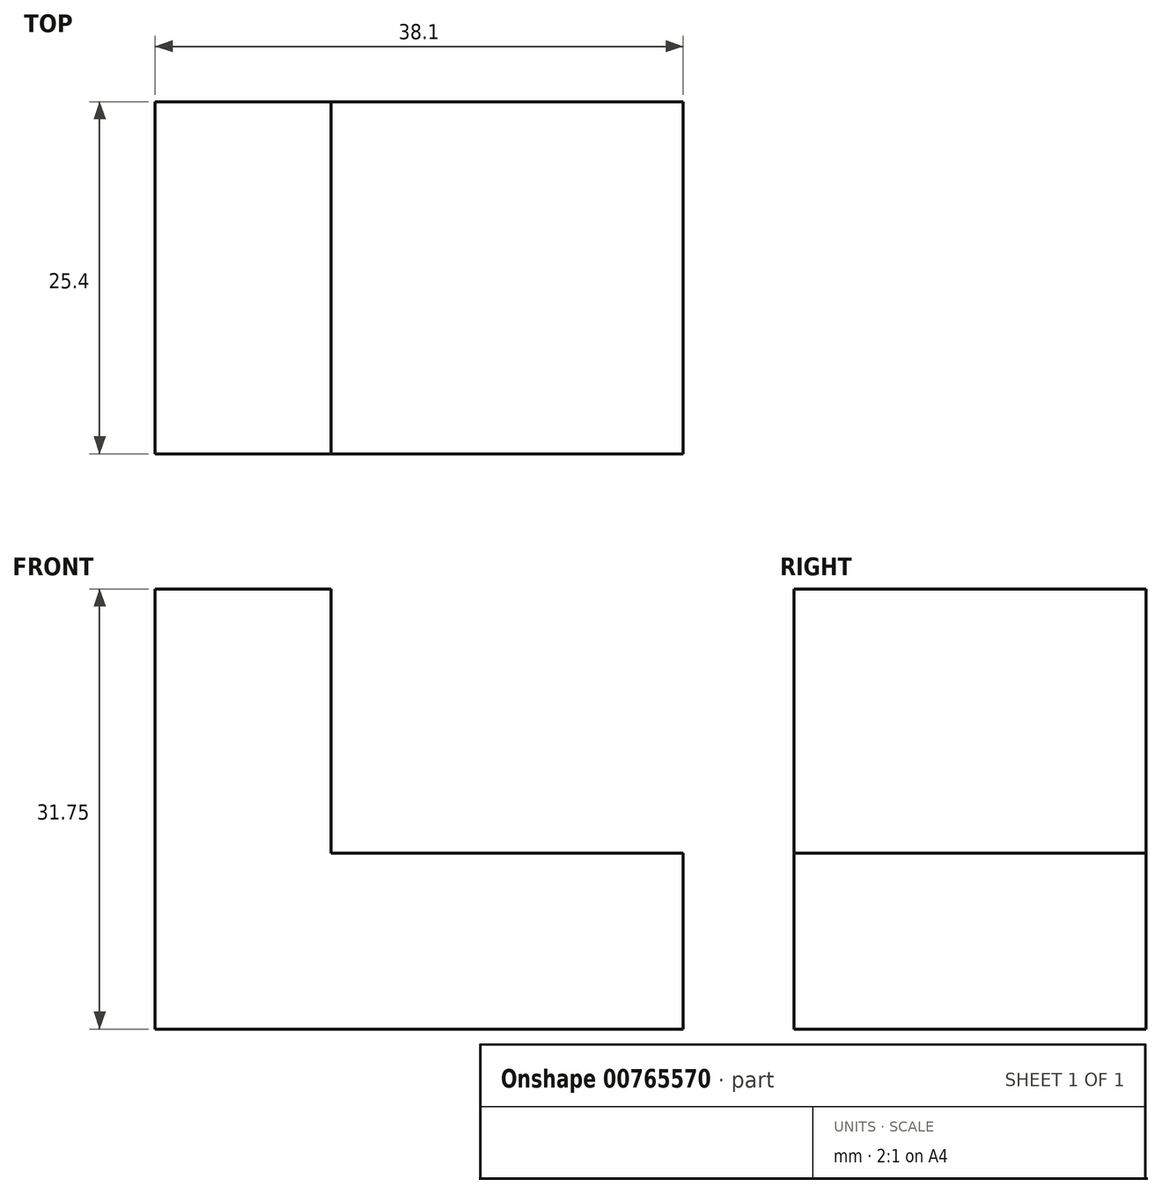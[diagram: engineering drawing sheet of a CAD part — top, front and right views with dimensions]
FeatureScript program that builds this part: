
annotation { "Feature Type Name" : "Feature", "Feature Type Description" : "" }
export const myFeature = defineFeature(function(context is Context, id is Id, definition is map)
    precondition{}
    {
        {
            var Q0;
            Q0=qCreatedBy(makeId("Front.planeOp"),FACE);
            var sketch = newSketch(context, id + "F0", { "sketchPlane" : qUnion([Q0])});
            skLineSegment(sketch, "E0", {"start": v(0, 0) * mm, "end": v(38.1, 0) * mm});
            skLineSegment(sketch, "E1", {"start": v(0, 0) * mm, "end": v(0, 31.75) * mm});
            skLineSegment(sketch, "E2", {"start": v(0, 31.75) * mm, "end": v(12.7, 31.75) * mm});
            skLineSegment(sketch, "E3", {"start": v(12.7, 31.75) * mm, "end": v(12.7, 12.7) * mm});
            skLineSegment(sketch, "E4", {"start": v(12.7, 12.7) * mm, "end": v(38.1, 12.7) * mm});
            skLineSegment(sketch, "E5", {"start": v(38.1, 0) * mm, "end": v(38.1, 12.7) * mm});
            skSolve(sketch);
        }
        {
            var Q0;
            Q0 = qSketchRegion(id + "F0", true);
            extrude(context, id + "F1", {"entities" : qUnion([Q0]), "depth" : 25.4 * mm, "offsetDistance" : 25.4 * mm});
        }
    });
